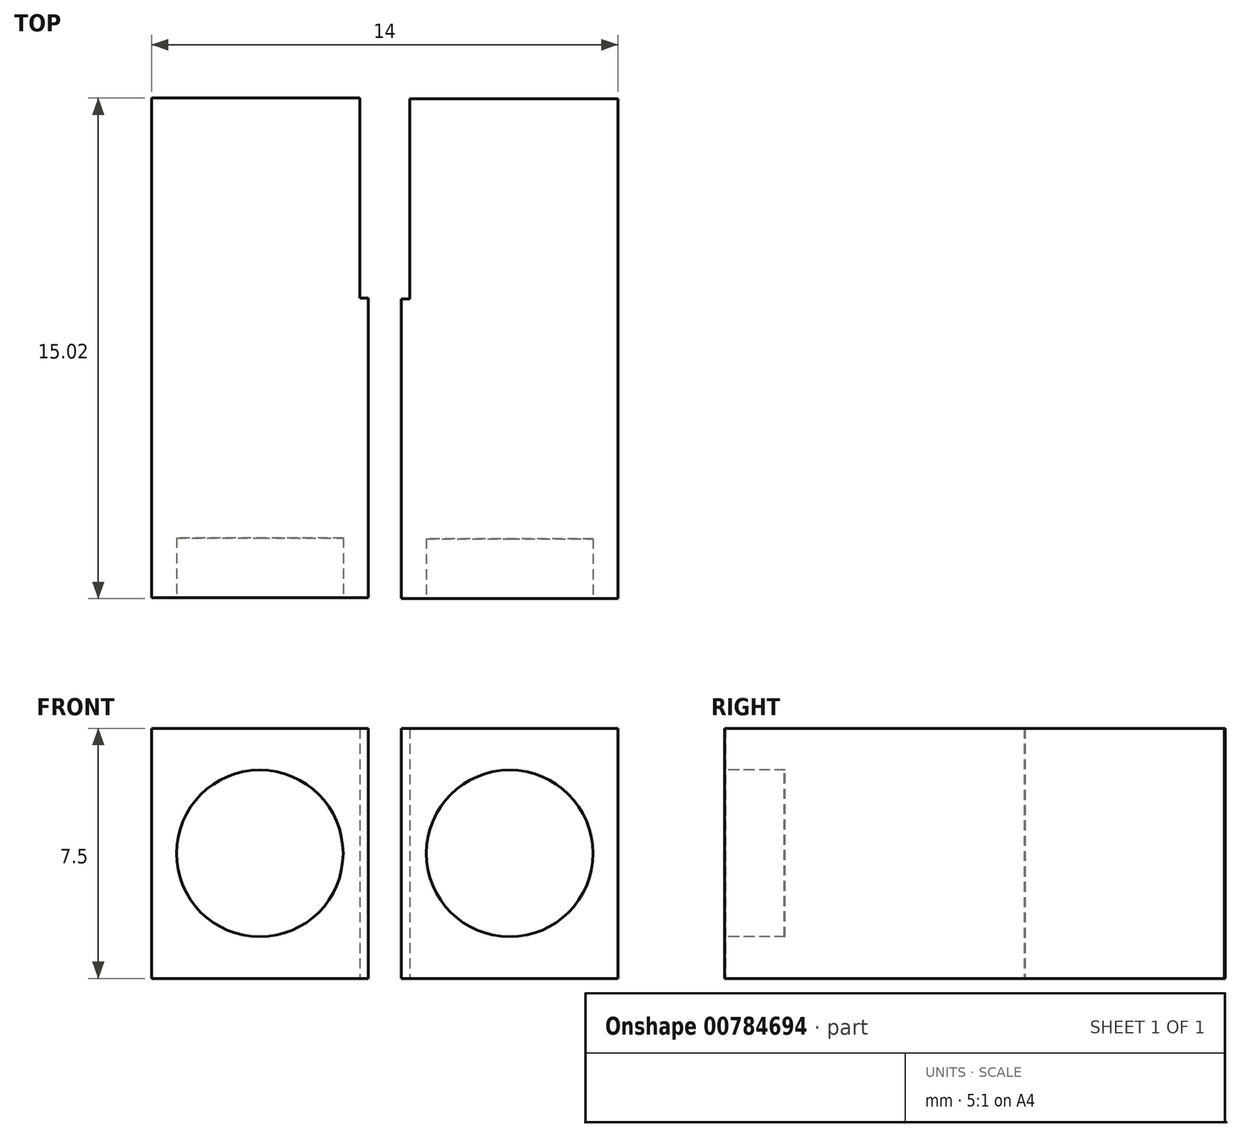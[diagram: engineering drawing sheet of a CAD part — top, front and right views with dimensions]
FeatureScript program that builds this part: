
annotation { "Feature Type Name" : "Feature", "Feature Type Description" : "" }
export const myFeature = defineFeature(function(context is Context, id is Id, definition is map)
    precondition{}
    {
        {
            var Q0;
            Q0=qCreatedBy(makeId("Top.planeOp"),FACE);
            var sketch = newSketch(context, id + "F0", { "sketchPlane" : qUnion([Q0])});
            skLineSegment(sketch, "E0", {"start": v(1.5, -0.02) * mm, "end": v(7.75, -0.02) * mm});
            skLineSegment(sketch, "E1", {"start": v(0, 0) * mm, "end": v(-6.25, 0) * mm});
            skLineSegment(sketch, "E2", {"start": v(-6.25, 0) * mm, "end": v(-6.25, -5) * mm});
            skLineSegment(sketch, "E3", {"start": v(7.75, -0.02) * mm, "end": v(7.75, -5.02) * mm});
            skLineSegment(sketch, "E4", {"start": v(-6.25, -5) * mm, "end": v(0, -5) * mm});
            skLineSegment(sketch, "E5", {"start": v(7.75, -5.02) * mm, "end": v(1.5, -5.02) * mm});
            skLineSegment(sketch, "E6", {"start": v(1.5, -5.02) * mm, "end": v(1.5, -6.02) * mm});
            skLineSegment(sketch, "E7", {"start": v(1.5, -6.02) * mm, "end": v(1.25, -6.02) * mm});
            skLineSegment(sketch, "E8", {"start": v(0, -5) * mm, "end": v(0, -6) * mm});
            skLineSegment(sketch, "E9", {"start": v(0, -6) * mm, "end": v(0.25, -6) * mm});
            skLineSegment(sketch, "E10", {"start": v(0.25, -6) * mm, "end": v(0.25, -12.5) * mm});
            skLineSegment(sketch, "E11", {"start": v(1.25, -6.02) * mm, "end": v(1.25, -12.52) * mm});
            skLineSegment(sketch, "E12", {"start": v(0, 0) * mm, "end": v(0, -5) * mm});
            skLineSegment(sketch, "E13", {"start": v(1.5, -0.02) * mm, "end": v(1.5, -5.02) * mm});
            skLineSegment(sketch, "E14", {"start": v(-6.25, -5) * mm, "end": v(-6.25, -12.5) * mm});
            skLineSegment(sketch, "E15", {"start": v(-6.25, -12.5) * mm, "end": v(0.25, -12.5) * mm});
            skLineSegment(sketch, "E16", {"start": v(7.75, -5.02) * mm, "end": v(7.75, -12.52) * mm});
            skLineSegment(sketch, "E17", {"start": v(7.75, -12.52) * mm, "end": v(1.25, -12.52) * mm});
            skLineSegment(sketch, "E18", {"start": v(-6.25, -12.5) * mm, "end": v(-6.25, -15) * mm});
            skLineSegment(sketch, "E19", {"start": v(0.25, -12.5) * mm, "end": v(0.25, -15) * mm});
            skLineSegment(sketch, "E20", {"start": v(0.25, -15) * mm, "end": v(-6.25, -15) * mm});
            skLineSegment(sketch, "E21", {"start": v(1.25, -12.52) * mm, "end": v(1.25, -15.02) * mm});
            skLineSegment(sketch, "E22", {"start": v(7.75, -12.52) * mm, "end": v(7.75, -15.02) * mm});
            skLineSegment(sketch, "E23", {"start": v(7.75, -15.02) * mm, "end": v(1.25, -15.02) * mm});
            skSolve(sketch);
        }
        {
            var Q0;
            Q0=makeQuery(id+"F0.imprint","IMPRINT",FACE,{"disambiguationData":[TD([[makeQuery(id+"F0.imprint","IMPRINT",EDGE,{"derivedFrom":sQuery(id+"F0.wireOp",EDGE,"E15")}),-1.0]])]});
            var Q1;
            Q1=makeQuery(id+"F0.imprint","IMPRINT",FACE,{"disambiguationData":[TD([[makeQuery(id+"F0.imprint","IMPRINT",EDGE,{"derivedFrom":sQuery(id+"F0.wireOp",EDGE,"E17")}),1.0]])]});
            var Q2;
            Q2=makeQuery(id+"F0.imprint","IMPRINT",FACE,{"disambiguationData":[TD([[makeQuery(id+"F0.imprint","IMPRINT",EDGE,{"derivedFrom":sQuery(id+"F0.wireOp",EDGE,"E4")}),-1.0]])]});
            var Q3;
            Q3=makeQuery(id+"F0.imprint","IMPRINT",FACE,{"disambiguationData":[TD([[makeQuery(id+"F0.imprint","IMPRINT",EDGE,{"derivedFrom":sQuery(id+"F0.wireOp",EDGE,"E5")}),1.0]])]});
            var Q4;
            Q4=makeQuery(id+"F0.imprint","IMPRINT",FACE,{"disambiguationData":[TD([[makeQuery(id+"F0.imprint","IMPRINT",EDGE,{"derivedFrom":sQuery(id+"F0.wireOp",EDGE,"E0")}),-1.0]])]});
            var Q5;
            Q5=makeQuery(id+"F0.imprint","IMPRINT",FACE,{"disambiguationData":[TD([[makeQuery(id+"F0.imprint","IMPRINT",EDGE,{"derivedFrom":sQuery(id+"F0.wireOp",EDGE,"E1")}),1.0]])]});
            extrude(context, id + "F1", {"entities" : qUnion([Q0, Q1, Q2, Q3, Q4, Q5]), "depth" : 7.5 * mm, "offsetDistance" : 25 * mm});
        }
        {
            var Q0;
            Q0=makeQuery(id+"F1.opExtrude","SWEPT_FACE",FACE,{"disambiguationData":[OSD([sQuery(id+"F0.wireOp",EDGE,"E20")])]});
            var sketch = newSketch(context, id + "F2", { "sketchPlane" : qUnion([Q0])});
            skPoint(sketch, "E24.start.orphan", {"position": v(-3, 7.5) * mm});
            skPoint(sketch, "E25", {"position": v(-3, 3.75) * mm});
            skCircle(sketch, "E26", {"center": v(-3, 3.75) * mm, "radius": 2.5 * mm});
            skSolve(sketch);
        }
        {
            var Q0;
            Q0=makeQuery(id+"F1.opExtrude","SWEPT_FACE",FACE,{"disambiguationData":[OSD([sQuery(id+"F0.wireOp",EDGE,"E23")])]});
            var sketch = newSketch(context, id + "F3", { "sketchPlane" : qUnion([Q0])});
            skPoint(sketch, "E27", {"position": v(4.5, 3.75) * mm});
            skPoint(sketch, "E28.start.orphan", {"position": v(4.5, 7.5) * mm});
            skCircle(sketch, "E29", {"center": v(4.5, 3.75) * mm, "radius": 2.5 * mm});
            skSolve(sketch);
        }
        {
            var Q0;
            Q0=makeQuery(id+"F2.imprint","IMPRINT",FACE,{"disambiguationData":[TD([[makeQuery(id+"F2.imprint","IMPRINT",EDGE,{"derivedFrom":sQuery(id+"F2.wireOp",EDGE,"E26")}),1.0]])]});
            var Q1;
            Q1=makeQuery(id+"F3.imprint","IMPRINT",FACE,{"disambiguationData":[TD([[makeQuery(id+"F3.imprint","IMPRINT",EDGE,{"derivedFrom":sQuery(id+"F3.wireOp",EDGE,"E29")}),1.0]])]});
            extrude(context, id + "F4", {"entities" : qUnion([Q0, Q1]), "operationType" : NewBodyOperationType.REMOVE, "oppositeDirection" : true, "depth" : 1.8 * mm, "offsetDistance" : 25 * mm});
        }
    });
